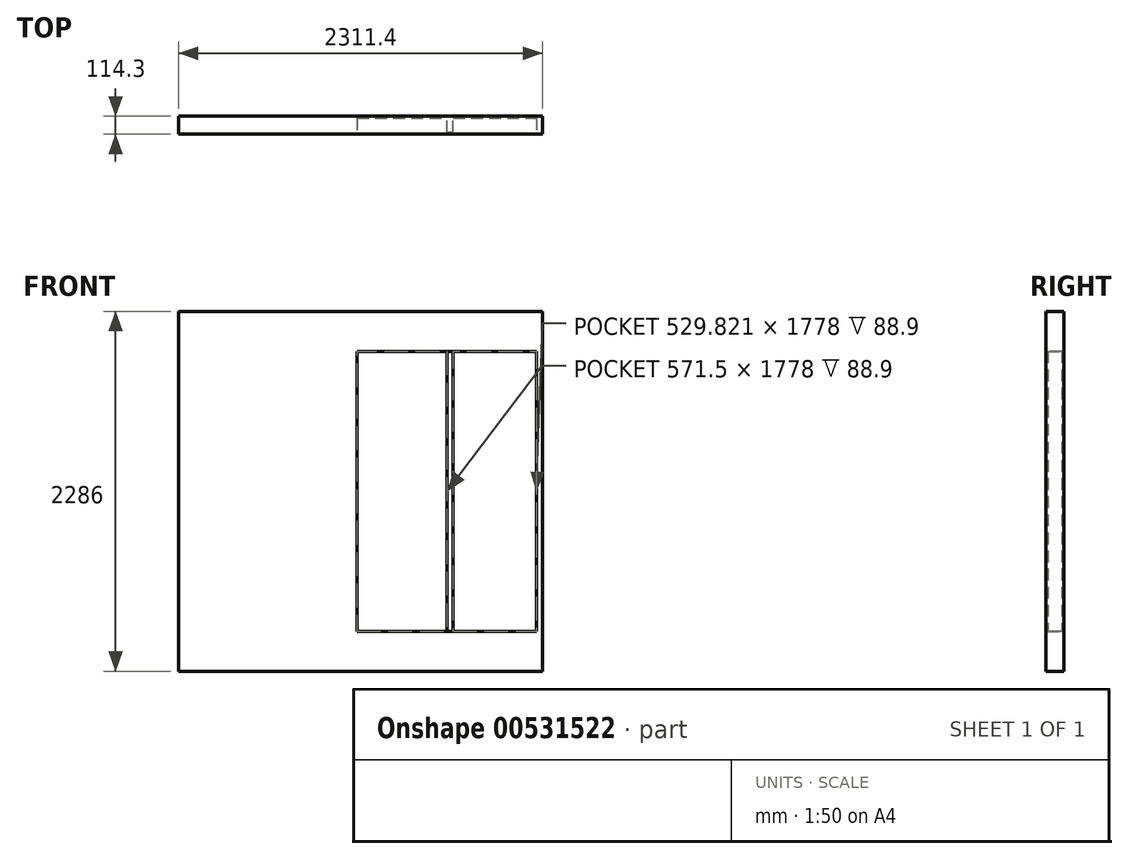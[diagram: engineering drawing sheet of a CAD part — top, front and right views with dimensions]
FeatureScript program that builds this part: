
annotation { "Feature Type Name" : "Feature", "Feature Type Description" : "" }
export const myFeature = defineFeature(function(context is Context, id is Id, definition is map)
    precondition{}
    {
        {
            var Q0;
            Q0=qCreatedBy(makeId("Front.planeOp"),FACE);
            var sketch = newSketch(context, id + "F0", { "sketchPlane" : qUnion([Q0])});
            skLineSegment(sketch, "E0.bottom", {"start": v(1155.7, 1143) * mm, "end": v(-1155.7, 1143) * mm});
            skLineSegment(sketch, "E0.top", {"start": v(1155.7, -1143) * mm, "end": v(-1155.7, -1143) * mm});
            skLineSegment(sketch, "E0.left", {"start": v(1155.7, 1143) * mm, "end": v(1155.7, -1143) * mm});
            skLineSegment(sketch, "E0.right", {"start": v(-1155.7, 1143) * mm, "end": v(-1155.7, -1143) * mm});
            skPoint(sketch, "E0.middle", {"position": v(0, 0) * mm});
            skSolve(sketch);
        }
        {
            var Q0;
            Q0 = qSketchRegion(id + "F0", true);
            extrude(context, id + "F1", {"entities" : qUnion([Q0]), "depth" : 114.3 * mm, "offsetDistance" : 25.4 * mm});
        }
        {
            var Q0;
            Q0=makeQuery(id+"F1.opExtrude","CAP_FACE",FACE,{"disambiguationData":[OSD([sQuery(id+"F0.wireOp",EDGE,"E0.bottom"),sQuery(id+"F0.wireOp",EDGE,"E0.top"),sQuery(id+"F0.wireOp",EDGE,"E0.left"),sQuery(id+"F0.wireOp",EDGE,"E0.right")])],"isStart":false});
            var sketch = newSketch(context, id + "F2", { "sketchPlane" : qUnion([Q0])});
            skLineSegment(sketch, "E1.bottom", {"start": v(-21.82, -889) * mm, "end": v(1117.6, -889) * mm});
            skLineSegment(sketch, "E1.top", {"start": v(-21.82, 889) * mm, "end": v(1117.6, 889) * mm});
            skLineSegment(sketch, "E1.left", {"start": v(-21.82, -889) * mm, "end": v(-21.82, 889) * mm});
            skLineSegment(sketch, "E1.right", {"start": v(1117.6, -889) * mm, "end": v(1117.6, 889) * mm});
            skSolve(sketch);
        }
        {
            var Q0;
            Q0 = qSketchRegion(id + "F2", true);
            extrude(context, id + "F3", {"entities" : qUnion([Q0]), "operationType" : NewBodyOperationType.REMOVE, "oppositeDirection" : true, "depth" : 101.6 * mm, "offsetDistance" : 25.4 * mm});
        }
        {
            var Q0;
            Q0=makeQuery(id+"F3.boolean.opBoolean","COPY",FACE,{"derivedFrom":makeQuery(id+"F3.opExtrude","CAP_FACE",FACE,{"disambiguationData":[OSD([sQuery(id+"F2.wireOp",EDGE,"E1.bottom"),sQuery(id+"F2.wireOp",EDGE,"E1.top"),sQuery(id+"F2.wireOp",EDGE,"E1.left"),sQuery(id+"F2.wireOp",EDGE,"E1.right")])],"isStart":false})});
            var sketch = newSketch(context, id + "F4", { "sketchPlane" : qUnion([Q0])});
            skLineSegment(sketch, "E2.bottom", {"start": v(549.68, 889) * mm, "end": v(587.78, 889) * mm});
            skLineSegment(sketch, "E2.top", {"start": v(549.68, -889) * mm, "end": v(587.78, -889) * mm});
            skLineSegment(sketch, "E2.left", {"start": v(549.68, 889) * mm, "end": v(549.68, -889) * mm});
            skLineSegment(sketch, "E2.right", {"start": v(587.78, 889) * mm, "end": v(587.78, -889) * mm});
            skSolve(sketch);
        }
        {
            var Q0;
            Q0 = qSketchRegion(id + "F4", true);
            extrude(context, id + "F5", {"entities" : qUnion([Q0]), "operationType" : NewBodyOperationType.ADD, "depth" : 88.9 * mm, "offsetDistance" : 25.4 * mm});
        }
    });
